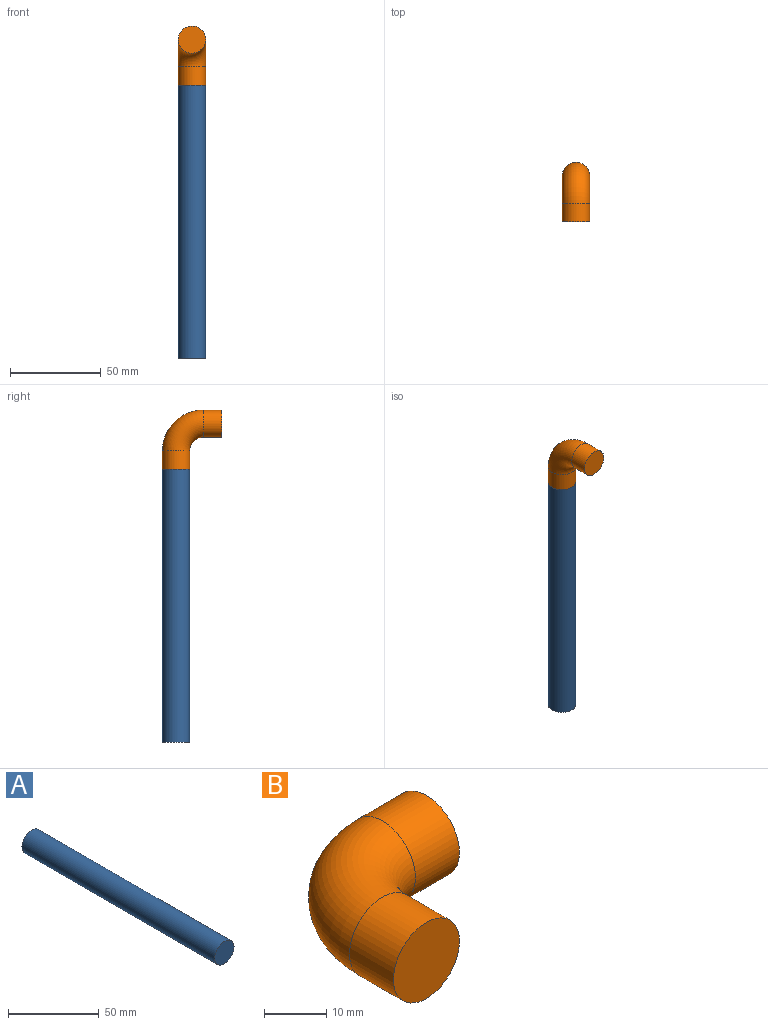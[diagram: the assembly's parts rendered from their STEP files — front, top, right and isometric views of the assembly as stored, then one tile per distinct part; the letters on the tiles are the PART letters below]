
ASSEMBLY  parts=2 mates=1
PART A: 3 faces, bbox 15x150x15 mm
  f0: cylinder r=7.5mm len=150mm, axis (0,1,0), area 7068.6mm2, adj f1,f2
  f1: plane 15x15mm, normal (0,-1,0), area 176.7mm2, adj f0
  f2: plane 15x15mm, normal (0,1,0), area 176.7mm2, adj f0
PART B: 5 faces, bbox 34.4x34.4x15 mm
  f0: plane 15x15mm, normal (0,-1,0), area 176.7mm2, adj f2
  f1: plane 15x15mm, normal (1,0,0), area 176.7mm2, adj f4
  f2: cylinder r=7.5mm len=15mm, axis (0,1,0), area 471.2mm2, adj f0,f3
  f3: torus R=15mm, axis (0,0,-1), area 1110.3mm2, adj f2,f4
  f4: cylinder r=7.5mm len=15mm, axis (1,0,0), area 471.2mm2, adj f1,f3
PLACE A rot(axis=(1,0,0),90deg) t=(15002.51,-872.43,-1350)mm
PLACE B rot(axis=(0.58,-0.58,-0.58),120deg) t=(14941.08,-909.02,-1350)mm
MATE fastened B.f2 <-> A.f0  axis (0,0,-1) through (14941.08,-909.02,-1350)mm
